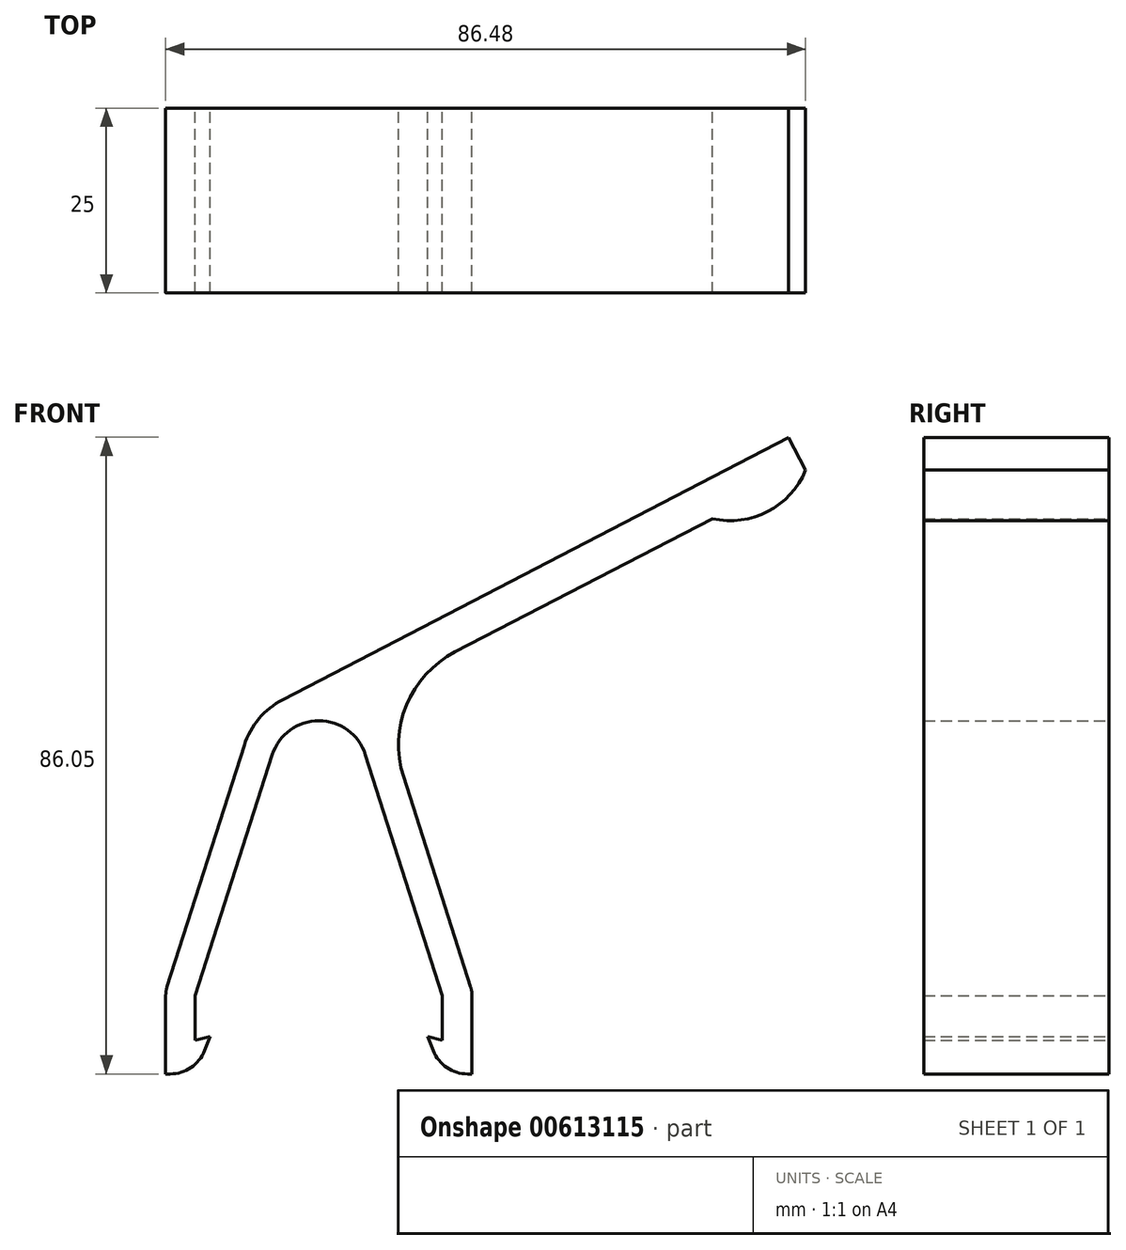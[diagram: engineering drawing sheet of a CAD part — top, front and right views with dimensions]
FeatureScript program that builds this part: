
annotation { "Feature Type Name" : "Feature", "Feature Type Description" : "" }
export const myFeature = defineFeature(function(context is Context, id is Id, definition is map)
    precondition{}
    {
        {
            var Q0;
            Q0=qCreatedBy(makeId("Front.planeOp"),FACE);
            var sketch = newSketch(context, id + "F0", { "sketchPlane" : qUnion([Q0])});
            skArc(sketch, "E0", {"start": v(6.29, 32.59) * mm, "mid": v(0, 37.18) * mm, "end": v(-6.29, 32.59) * mm});
            skLineSegment(sketch, "E1", {"start": v(6.29, 32.59) * mm, "end": v(16.7, 0) * mm});
            skLineSegment(sketch, "E2", {"start": v(-6.29, 32.59) * mm, "end": v(-16.7, 0) * mm});
            skLineSegment(sketch, "E3.0", {"start": v(-10.08, 33.86) * mm, "end": v(-20.51, 1.22) * mm});
            skLineSegment(sketch, "E4.0", {"start": v(11.44, 29.6) * mm, "end": v(20.51, 1.22) * mm});
            skArc(sketch, "E5", {"start": v(-4.87, 40.03) * mm, "mid": v(-8.1, 37.46) * mm, "end": v(-10.08, 33.86) * mm});
            skLineSegment(sketch, "E6.bottom", {"start": v(-16.7, 0) * mm, "end": v(-20.7, 0) * mm});
            skLineSegment(sketch, "E6.top", {"start": v(-16.7, -10.56) * mm, "end": v(-20.7, -10.56) * mm});
            skLineSegment(sketch, "E6.left", {"start": v(-16.7, 0) * mm, "end": v(-16.7, -10.56) * mm});
            skLineSegment(sketch, "E6.right", {"start": v(-20.7, 0) * mm, "end": v(-20.7, -10.56) * mm});
            skLineSegment(sketch, "E7.bottom", {"start": v(16.7, 0) * mm, "end": v(20.7, 0) * mm});
            skLineSegment(sketch, "E7.top", {"start": v(16.7, -10.56) * mm, "end": v(20.7, -10.56) * mm});
            skLineSegment(sketch, "E7.left", {"start": v(16.7, 0) * mm, "end": v(16.7, -10.56) * mm});
            skLineSegment(sketch, "E7.right", {"start": v(20.7, 0) * mm, "end": v(20.7, -10.56) * mm});
            skArc(sketch, "E8", {"start": v(-20.51, 1.22) * mm, "mid": v(-20.65, 0.62) * mm, "end": v(-20.7, 0) * mm});
            skArc(sketch, "E9", {"start": v(20.7, 0) * mm, "mid": v(20.65, 0.62) * mm, "end": v(20.51, 1.22) * mm});
            skLineSegment(sketch, "E10", {"start": v(-4.87, 40.03) * mm, "end": v(63.48, 75.49) * mm});
            skLineSegment(sketch, "E11", {"start": v(63.48, 75.49) * mm, "end": v(65.78, 71.05) * mm});
            skLineSegment(sketch, "E12", {"start": v(65.78, 71.05) * mm, "end": v(18.41, 46.48) * mm});
            skArc(sketch, "E13", {"start": v(18.41, 46.48) * mm, "mid": v(11.84, 39.31) * mm, "end": v(11.44, 29.6) * mm});
            skArc(sketch, "E14", {"start": v(53.16, 64.5) * mm, "mid": v(60.67, 65.47) * mm, "end": v(65.78, 71.05) * mm});
            skLineSegment(sketch, "E15.left", {"start": v(-16.7, -5.28) * mm, "end": v(-16.7, -10.56) * mm});
            skLineSegment(sketch, "E16.left", {"start": v(16.7, -5.28) * mm, "end": v(16.7, -10.56) * mm});
            skLineSegment(sketch, "E17", {"start": v(14.7, -5.47) * mm, "end": v(16.7, -10.56) * mm});
            skLineSegment(sketch, "E18", {"start": v(14.7, -5.47) * mm, "end": v(16.7, -6.03) * mm});
            skLineSegment(sketch, "E19", {"start": v(-14.7, -5.52) * mm, "end": v(-16.7, -6.03) * mm});
            skLineSegment(sketch, "E20", {"start": v(-14.7, -5.52) * mm, "end": v(-16.7, -10.56) * mm});
            skSolve(sketch);
        }
        {
            var Q0;
            Q0=makeQuery(id+"F0.imprint","IMPRINT",FACE,{"disambiguationData":[TD([[makeQuery(id+"F0.imprint","IMPRINT",EDGE,{"derivedFrom":sQuery(id+"F0.wireOp",EDGE,"E0")}),-1.0]])]});
            var Q1;
            {var subQ3=sQuery(id+"F0.wireOp",EDGE,"E6.bottom");Q1=makeQuery(id+"F0.imprint","IMPRINT",FACE,{"disambiguationData":[TD([[makeQuery(id+"F0.imprint","IMPRINT",EDGE,{"derivedFrom":subQ3}),1.0]])]});}
            var Q2;
            {var subQ2=sQuery(id+"F0.wireOp",EDGE,"lhKcUkHS-TPyC-bHln-YaZt-UGc8A8o2h55p");Q2=makeQuery(id+"F0.imprint","IMPRINT",FACE,{"disambiguationData":[TD([[makeQuery(id+"F0.imprint","IMPRINT",EDGE,{"derivedFrom":subQ2}),-1.0]])]});}
            var Q3;
            {var subQ3=sQuery(id+"F0.wireOp",EDGE,"E7.bottom");Q3=makeQuery(id+"F0.imprint","IMPRINT",FACE,{"disambiguationData":[TD([[makeQuery(id+"F0.imprint","IMPRINT",EDGE,{"derivedFrom":subQ3}),-1.0]])]});}
            var Q4;
            {var subQ2=sQuery(id+"F0.wireOp",EDGE,"QtlHALiW-eprS-10bY-h6zf-lwsfpy6kj2Ga");Q4=makeQuery(id+"F0.imprint","IMPRINT",FACE,{"disambiguationData":[TD([[makeQuery(id+"F0.imprint","IMPRINT",EDGE,{"derivedFrom":subQ2}),1.0]])]});}
            var Q5;
            {var subQ0=sQuery(id+"F0.wireOp",EDGE,"0WLrn2QH-vDmy-BqSr-Ph8w-ZvOjHOHh7UpQ");Q5=makeQuery(id+"F0.imprint","IMPRINT",FACE,{"disambiguationData":[TD([[makeQuery(id+"F0.imprint","IMPRINT",EDGE,{"derivedFrom":subQ0}),1.0]])]});}
            var Q6;
            {var subQ0=sQuery(id+"F0.wireOp",EDGE,"E14");Q6=makeQuery(id+"F0.imprint","IMPRINT",FACE,{"disambiguationData":[TD([[makeQuery(id+"F0.imprint","IMPRINT",EDGE,{"derivedFrom":subQ0}),1.0]])]});}
            var Q7;
            Q7=makeQuery(id+"F0.imprint","IMPRINT",FACE,{"disambiguationData":[TD([[makeQuery(id+"F0.imprint","IMPRINT",EDGE,{"derivedFrom":sQuery(id+"F0.wireOp",EDGE,"E15.bottom")}),-1.0]])]});
            var Q8;
            Q8=makeQuery(id+"F0.imprint","IMPRINT",FACE,{"disambiguationData":[TD([[makeQuery(id+"F0.imprint","IMPRINT",EDGE,{"derivedFrom":sQuery(id+"F0.wireOp",EDGE,"E16.bottom")}),1.0]])]});
            var Q9;
            {var subQ1=sQuery(id+"F0.wireOp",EDGE,"E15.left");var subQ3=sQuery(id+"F0.wireOp",EDGE,"E19");var subQ4=makeQuery(id+"F0.imprint","INTERSECT",VERTEX,{"derivedFrom":[subQ1,subQ3]});Q9=makeQuery(id+"F0.imprint","IMPRINT",FACE,{"disambiguationData":[TD([[makeQuery(id+"F0.imprint","IMPRINT",EDGE,{"disambiguationData":[TD([[subQ4,1.0]])],"derivedFrom":subQ3}),1.0]])]});}
            var Q10;
            {var subQ0=sQuery(id+"F0.wireOp",EDGE,"E17");Q10=makeQuery(id+"F0.imprint","IMPRINT",FACE,{"disambiguationData":[TD([[makeQuery(id+"F0.imprint","IMPRINT",EDGE,{"derivedFrom":subQ0}),1.0]])]});}
            extrude(context, id + "F1", {"entities" : qUnion([Q0, Q1, Q2, Q3, Q4, Q5, Q6, Q7, Q8, Q9, Q10]), "endBound" : BoundingType.SYMMETRIC, "depth" : 25 * mm, "offsetDistance" : 25 * mm});
        }
        {
            var Q0;
            Q0=makeQuery(id+"F1.opExtrude","SWEPT_EDGE",EDGE,{"disambiguationData":[OSD([sQuery(id+"F0.wireOp",EDGE,"4Jb99seA-huRH-p29Z-Tf1s-Rb8DBsahbhtd"),sQuery(id+"F0.wireOp",EDGE,"eBBCAWyS-3Dbi-ui7h-iKW4-UdJJ69oEjymj"),sQuery(id+"F0.wireOp",EDGE,"0WLrn2QH-vDmy-BqSr-Ph8w-ZvOjHOHh7UpQ")])]});
            var Q1;
            Q1=makeQuery(id+"F1.opExtrude","SWEPT_EDGE",EDGE,{"disambiguationData":[OSD([sQuery(id+"F0.wireOp",EDGE,"E15.top"),sQuery(id+"F0.wireOp",EDGE,"E15.right")])]});
            var Q2;
            Q2=makeQuery(id+"F1.opExtrude","SWEPT_EDGE",EDGE,{"disambiguationData":[OSD([sQuery(id+"F0.wireOp",EDGE,"E16.top"),sQuery(id+"F0.wireOp",EDGE,"E16.right")])]});
            var Q3;
            Q3=makeQuery(id+"F1.opExtrude","SWEPT_EDGE",EDGE,{"disambiguationData":[OSD([sQuery(id+"F0.wireOp",EDGE,"E7.top"),sQuery(id+"F0.wireOp",EDGE,"E16.left"),sQuery(id+"F0.wireOp",EDGE,"E17")])]});
            var Q4;
            Q4=makeQuery(id+"F1.opExtrude","SWEPT_EDGE",EDGE,{"disambiguationData":[OSD([sQuery(id+"F0.wireOp",EDGE,"E6.top"),sQuery(id+"F0.wireOp",EDGE,"E15.left"),sQuery(id+"F0.wireOp",EDGE,"E20")])]});
            fillet(context, id + "F2", {"entities" : qUnion([Q0, Q1, Q2, Q3, Q4]), "radius" : 5 * mm, "tangentPropagation" : true, "allowEdgeOverflow" : false});
        }
    });
